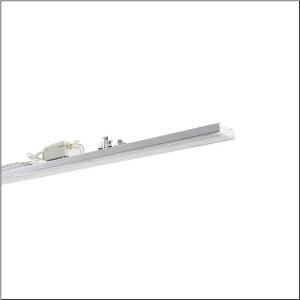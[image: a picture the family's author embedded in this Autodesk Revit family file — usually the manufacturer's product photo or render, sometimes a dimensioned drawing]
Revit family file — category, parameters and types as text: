
# Revit family: licross_11_recessed_mo_51te14cn485g
name_source: partatom
category: Lighting Fixtures
units: mm (PartAtom-declared; Revit-internal decimal feet)

## family parameters
Cut with Voids When Loaded = No
Host = Face
Light Source = No
Part Type = Normal
Room Calculation Point = No
Round Connector Dimension = Use Diameter
Shared = No

## types (1)
- --- (1 x LED, 8570 lm, 49.3 W, 4000K)
    Apparent Load = 49 VA
    CIE Flux Codes = 56 84 97 100 100
    Color Rendering = 80
    Color Temperature = 4000K
    Default Elevation = 1800 mm
    Description = Licross 11 Recessed MO, luminaire insert, of sheet steel, galvanised, coil coated, white, length: 1.500mm, width: 66mm, height: 67mm, LED rated luminous flux: 8.570lm, light colour: 840, SDCM (Standard Deviation of Colour Matching)MacAdam ≤ 2 SDCM (initial), control gear: ON/OFF Multilumen, CLOi, with plug, 3-pole, with phase selection, mains connection: 220..240V, AC, 50/60Hz, start of lifetime: 49W, end of service life: 55W, internal wiring halogen-free, primary light control with lens, of plastic, primary optical cover: cover, of PMMA, light emission: direct distribution, primary light characteristic: asymmetric, protection rating (complete): IP54, insulation class (complete): insulation class I (protective earthing), certification: CE, ENEC, VDE, UKCA, protection symbol: D if used in an environment with non-conductive dust loads with corresponding accessories, impact resistance: IK06, permissible ambient temperature for indoor applications: -35..+40°C, corresponds to IFS (International Featured Standards) requirements for safety and quality in the food industry, reducing of maximum allowable ambient temperature of 5°C with ceiling mounting, LABS conformity tested according to VDMA 24364:2018-05, The light source and the operating device comply with the requirements of the Ecodesign Regulation (EU) 2019/2020 and are replaceable in accordance with this regulation, packaging unit: 1 piece
    Height = 58 mm
    Lamp = 1 x LED
    Lamp Light Flux = 8570 lm
    Lamp Power = 49.3 W
    Lamp count = 1
    Length = 1500 mm
    Luminous efficacy = 174 lm/W
    Manufacturer = Siteco
    ModVariant = No
    Model = 51TE14CN485G
    Mounting Place = Ceiling
    Mounting Type = Pendant
    Number of Poles = 1
    OnlyDefault = Yes
    Power Factor = 1
    Product Name = Licross 11 Recessed MO
    Product group = luminaire insert | ceiling pendant
    ProductGroupID = 901
    Protection Class = Protection class I
    Protection Degree = IP 54
    RLX_Detail_Level = 1
    RLX_Emergency_Light_Flux = 0 lm
    RLX_Emergency_Type = 0
    RLX_Emergency_Type_DB = No
    RlxData = <blob elided: 23097 chars, md5=96e7ee23>
    Socket = socket
    Standby Power = 0 W
    System Light Flux = 8570 lm
    System Power = 49 W
    Type Comments = factory setting: luminous flux: 100 % | (A | C | E) | 113 mA
    Type Image = l_1296930.jpg
    URL = http://relux.com
    VarID = @adj_000453
    Voltage = 0 V
    Weight = 0.00 kg
    Width = 66 mm

## geometry (parser evidence)
native form markers: Blend x4, Sweep x11
no freeform markers — native parametric forms only
